# Revit family: Haworth_Cappellini_Smoke_ServiceTable_EU_PRELIMINARY
name_source: partatom
category: Furniture
revit_build: Autodesk Revit 2018 (Build: 20170223_1515(x64)
units: mm (PartAtom-declared; Revit-internal decimal feet)

## family parameters
Always vertical = Yes
Cut with Voids When Loaded = No
OmniClass Number = 23.40.70.14.64.21
OmniClass Title = Systems Furniture
Room Calculation Point = No
Shared = No
Work Plane-Based = No

## types (2) — shared parameters
Actual Height = 44 cm
Actual Width = 100 cm
Assembly Code = E2020200
Base Finish = Haworth _ Glass _ Clear
Description = Haworth - Cappellini - Service Table - Smoke
Manufacturer = Haworth
Model = SM_X
Revision Number = 1
Side Bottom Height = 21 cm
Size = Verify Final Dim. w/Haworth
Table Top Thickness = 1 cm
URL = https://www.haworth.com
URL - Product = https://www.haworth.com
Warranty = http://www.haworth.com
zero-valued in all types: Chamfer

## per-type parameters (varying)
| type | Actual Depth | Rectangle | Square |
| 100w x 100d - Square | 100 cm | No | Yes |
| 100w x 60d - Rectangle | 60 cm | Yes | No |

## geometry (parser evidence)
native form markers: Sweep x2
no freeform markers — native parametric forms only
